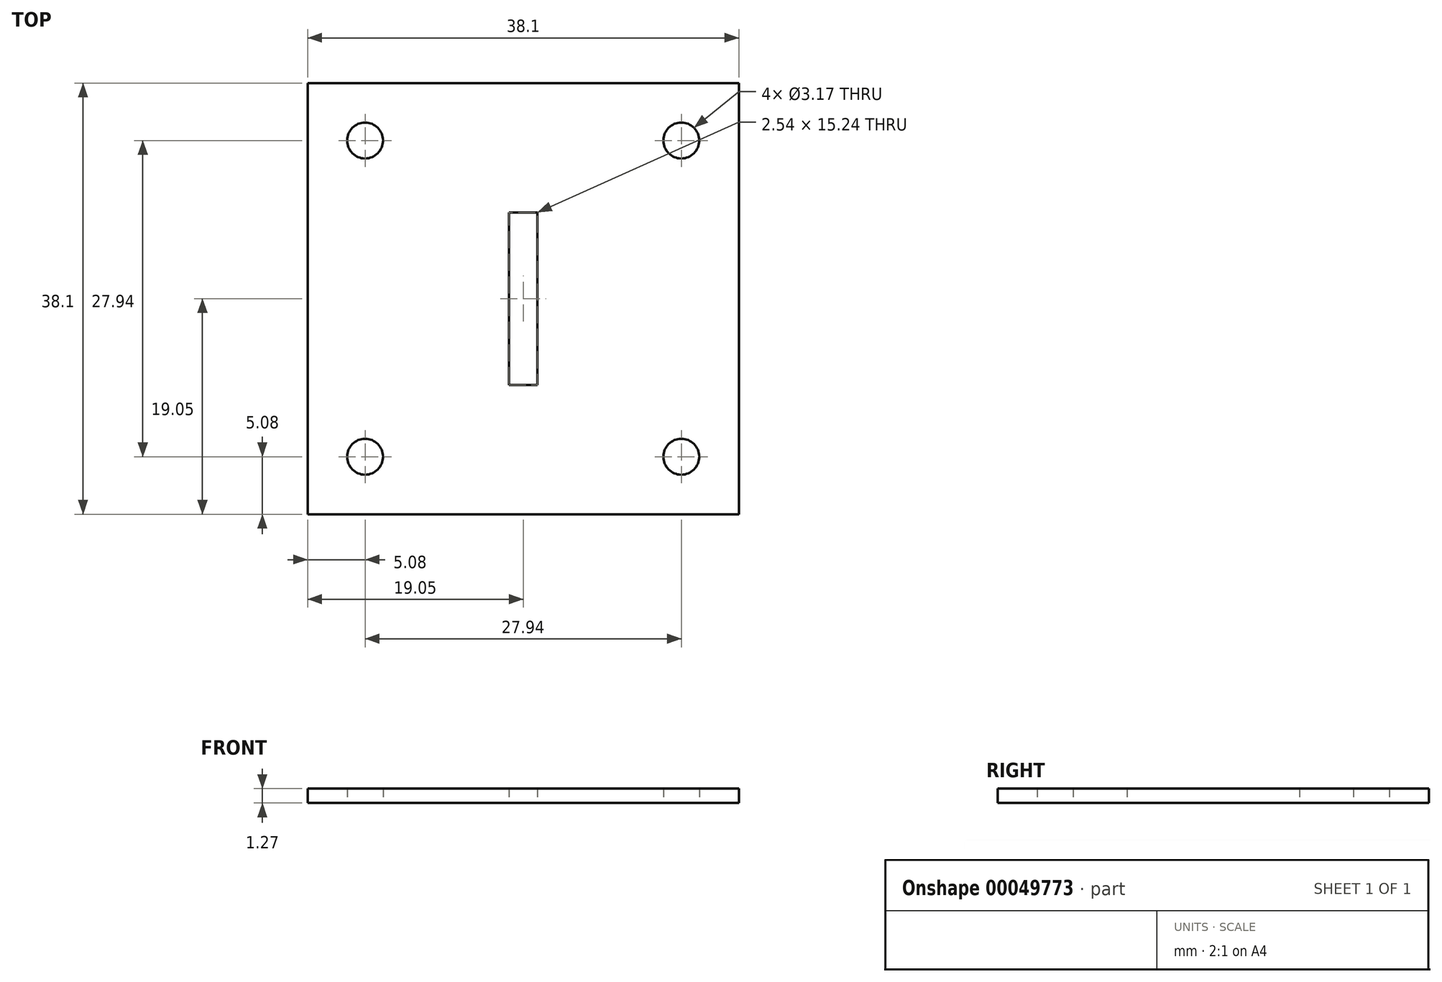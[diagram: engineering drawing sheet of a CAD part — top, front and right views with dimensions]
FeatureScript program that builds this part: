
annotation { "Feature Type Name" : "Feature", "Feature Type Description" : "" }
export const myFeature = defineFeature(function(context is Context, id is Id, definition is map)
    precondition{}
    {
        {
            var Q0;
            Q0=qCreatedBy(makeId("Top.planeOp"),FACE);
            var sketch = newSketch(context, id + "F0", { "sketchPlane" : qUnion([Q0])});
            skLineSegment(sketch, "E0.rect.bottom", {"start": v(19.05, -19.05) * mm, "end": v(-19.05, -19.05) * mm});
            skLineSegment(sketch, "E0.rect.top", {"start": v(19.05, 19.05) * mm, "end": v(-19.05, 19.05) * mm});
            skLineSegment(sketch, "E0.rect.left", {"start": v(19.05, -19.05) * mm, "end": v(19.05, 19.05) * mm});
            skLineSegment(sketch, "E0.rect.right", {"start": v(-19.05, -19.05) * mm, "end": v(-19.05, 19.05) * mm});
            skPoint(sketch, "E0.rect.middle", {"position": v(0, 0) * mm});
            skSolve(sketch);
        }
        {
            var Q0;
            Q0=qSketchRegion(id+"F0",true);
            extrude(context, id + "F1", {"entities" : qUnion([Q0]), "depth" : 1.27 * mm});
        }
        {
            var Q0;
            Q0=qCreatedBy(makeId("Top.planeOp"),FACE);
            var sketch = newSketch(context, id + "F3", { "sketchPlane" : qUnion([Q0])});
            skCircle(sketch, "E1", {"center": v(13.97, 13.97) * mm, "radius": 1.59 * mm});
            skSolve(sketch);
        }
        {
            var Q0;
            Q0=qSketchRegion(id+"F3",true);
            extrude(context, id + "F4", {"entities" : qUnion([Q0]), "operationType" : NewBodyOperationType.REMOVE, "depth" : 25.4 * mm});
        }
        {
            var Q0;
            Q0=makeQuery(id+"F1.opExtrude","SWEPT_BODY",BODY,{"disambiguationData":[OSD([sQuery(id+"F0.wireOp",EDGE,"E0.rect.bottom"),sQuery(id+"F0.wireOp",EDGE,"E0.rect.top"),sQuery(id+"F0.wireOp",EDGE,"E0.rect.left"),sQuery(id+"F0.wireOp",EDGE,"E0.rect.right")])]});
            var Q1;
            Q1=qCreatedBy(makeId("Right.planeOp"),FACE);
            mirror(context, id + "F5", {"operationType" : NewBodyOperationType.INTERSECT, "entities" : qUnion([Q0]), "mirrorPlane" : qUnion([Q1])});
        }
        {
            var Q0;
            Q0=makeQuery(id+"F1.opExtrude","SWEPT_BODY",BODY,{"disambiguationData":[OSD([sQuery(id+"F0.wireOp",EDGE,"E0.rect.bottom"),sQuery(id+"F0.wireOp",EDGE,"E0.rect.top"),sQuery(id+"F0.wireOp",EDGE,"E0.rect.left"),sQuery(id+"F0.wireOp",EDGE,"E0.rect.right")])]});
            var Q1;
            Q1=qCreatedBy(makeId("Front.planeOp"),FACE);
            mirror(context, id + "F6", {"operationType" : NewBodyOperationType.INTERSECT, "entities" : qUnion([Q0]), "mirrorPlane" : qUnion([Q1])});
        }
        {
            var Q0;
            Q0=qCreatedBy(makeId("Top.planeOp"),FACE);
            var sketch = newSketch(context, id + "F7", { "sketchPlane" : qUnion([Q0])});
            skLineSegment(sketch, "E2", {"start": v(-7.6, -0.64) * mm, "end": v(-7.6, -0.64) * mm});
            skLineSegment(sketch, "E3", {"start": v(-0.63, -7.6) * mm, "end": v(-0.63, -7.6) * mm});
            skLineSegment(sketch, "E4", {"start": v(-0.42, -5.06) * mm, "end": v(-0.42, -5.06) * mm});
            skLineSegment(sketch, "E5", {"start": v(0.42, -5.06) * mm, "end": v(0.42, -5.06) * mm});
            skLineSegment(sketch, "E6.rect.bottom", {"start": v(-1.27, -7.62) * mm, "end": v(1.27, -7.62) * mm});
            skLineSegment(sketch, "E6.rect.top", {"start": v(-1.27, 7.62) * mm, "end": v(1.27, 7.62) * mm});
            skLineSegment(sketch, "E6.rect.left", {"start": v(-1.27, -7.62) * mm, "end": v(-1.27, 7.62) * mm});
            skLineSegment(sketch, "E6.rect.right", {"start": v(1.27, -7.62) * mm, "end": v(1.27, 7.62) * mm});
            skSolve(sketch);
        }
        {
            var Q0;
            Q0=qSketchRegion(id+"F7",true);
            extrude(context, id + "F8", {"entities" : qUnion([Q0]), "operationType" : NewBodyOperationType.REMOVE, "depth" : 25.4 * mm});
        }
    });
